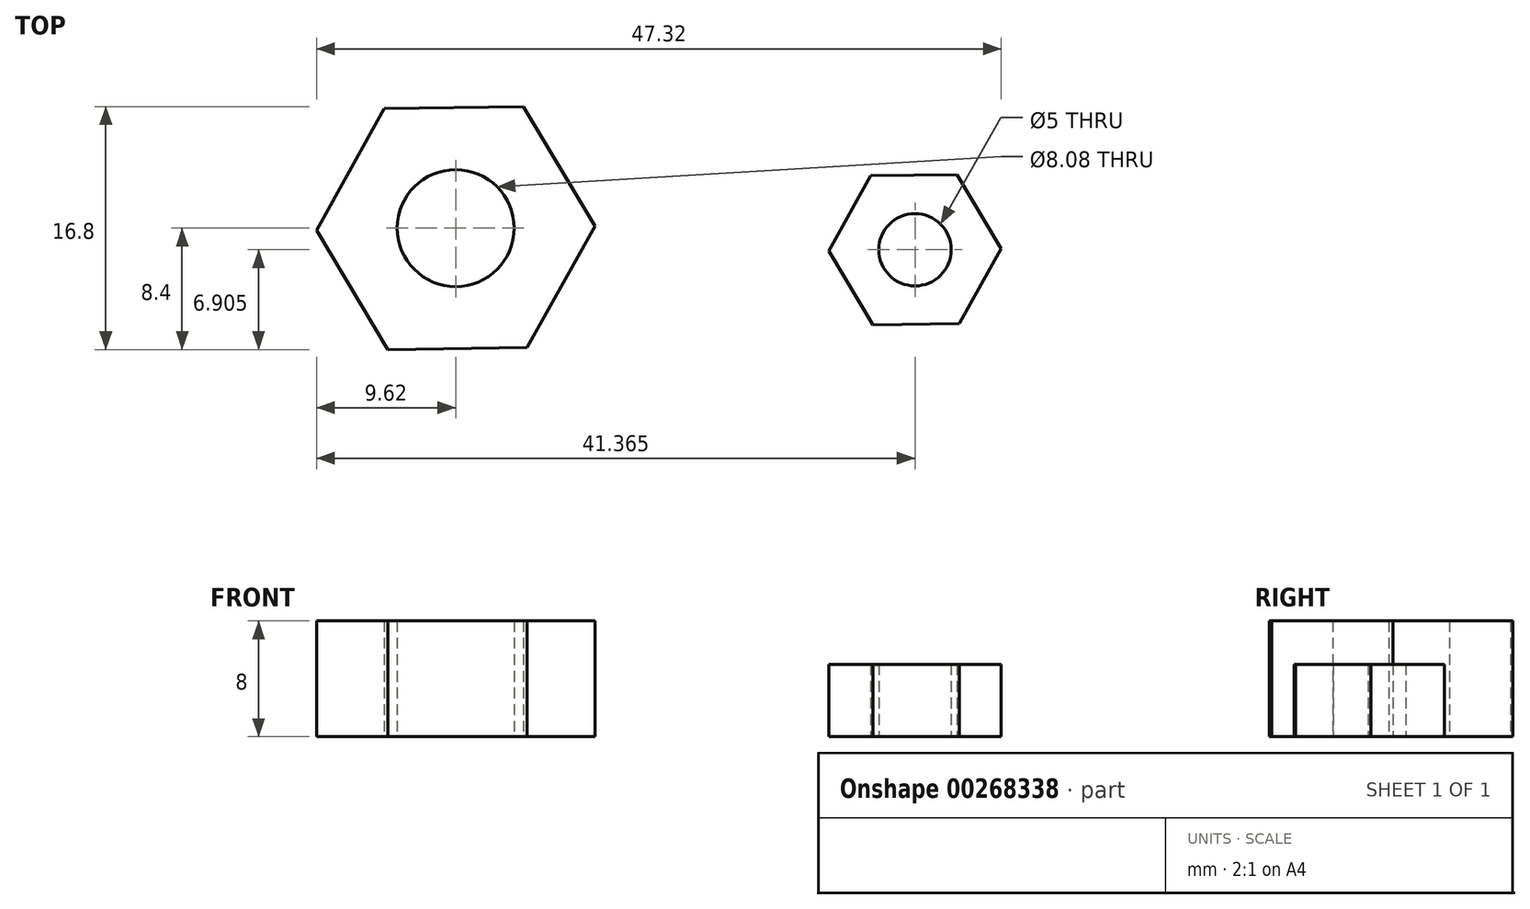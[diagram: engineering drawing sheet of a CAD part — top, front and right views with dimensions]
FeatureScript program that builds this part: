
annotation { "Feature Type Name" : "Feature", "Feature Type Description" : "" }
export const myFeature = defineFeature(function(context is Context, id is Id, definition is map)
    precondition{}
    {
        {
            var Q0;
            Q0=qCreatedBy(makeId("Top.planeOp"),FACE);
            var sketch = newSketch(context, id + "F0", { "sketchPlane" : qUnion([Q0])});
            skCircle(sketch, "E0.cCircle", {"center": v(0, 0) * mm, "radius": 8.33 * mm, "construction": true});
            skLineSegment(sketch, "E0.0", {"start": v(4.69, 8.4) * mm, "end": v(9.62, 0.14) * mm});
            skLineSegment(sketch, "E0.1", {"start": v(9.62, 0.14) * mm, "end": v(4.93, -8.26) * mm});
            skLineSegment(sketch, "E0.2", {"start": v(4.93, -8.26) * mm, "end": v(-4.69, -8.4) * mm});
            skLineSegment(sketch, "E0.3", {"start": v(-4.69, -8.4) * mm, "end": v(-9.62, -0.14) * mm});
            skLineSegment(sketch, "E0.4", {"start": v(-9.62, -0.14) * mm, "end": v(-4.93, 8.26) * mm});
            skLineSegment(sketch, "E0.5", {"start": v(-4.93, 8.26) * mm, "end": v(4.69, 8.4) * mm});
            skPoint(sketch, "E0.0.midPoint", {"position": v(7.15, 4.27) * mm});
            skCircle(sketch, "E1", {"center": v(0, 0) * mm, "radius": 4.04 * mm});
            skSolve(sketch);
        }
        {
            var Q0;
            Q0=qSketchRegion(id+"F0",true);
            extrude(context, id + "F1", {"entities" : qUnion([Q0]), "depth" : 8 * mm});
        }
        {
            var Q0;
            Q0=qCreatedBy(makeId("Top.planeOp"),FACE);
            var sketch = newSketch(context, id + "F2", { "sketchPlane" : qUnion([Q0])});
            skCircle(sketch, "E2.cCircle", {"center": v(31.75, -1.5) * mm, "radius": 5.16 * mm, "construction": true});
            skLineSegment(sketch, "E2.0", {"start": v(34.64, 3.7) * mm, "end": v(37.7, -1.4) * mm});
            skLineSegment(sketch, "E2.1", {"start": v(37.7, -1.4) * mm, "end": v(34.8, -6.6) * mm});
            skLineSegment(sketch, "E2.2", {"start": v(34.8, -6.6) * mm, "end": v(28.85, -6.7) * mm});
            skLineSegment(sketch, "E2.3", {"start": v(28.85, -6.7) * mm, "end": v(25.8, -1.58) * mm});
            skLineSegment(sketch, "E2.4", {"start": v(25.8, -1.58) * mm, "end": v(28.7, 3.62) * mm});
            skLineSegment(sketch, "E2.5", {"start": v(28.7, 3.62) * mm, "end": v(34.64, 3.7) * mm});
            skPoint(sketch, "E2.0.midPoint", {"position": v(36.17, 1.15) * mm});
            skCircle(sketch, "E3", {"center": v(31.75, -1.5) * mm, "radius": 2.5 * mm});
            skSolve(sketch);
        }
        {
            var Q0;
            Q0=qSketchRegion(id+"F2",true);
            extrude(context, id + "F3", {"entities" : qUnion([Q0]), "depth" : 5 * mm});
        }
    });
